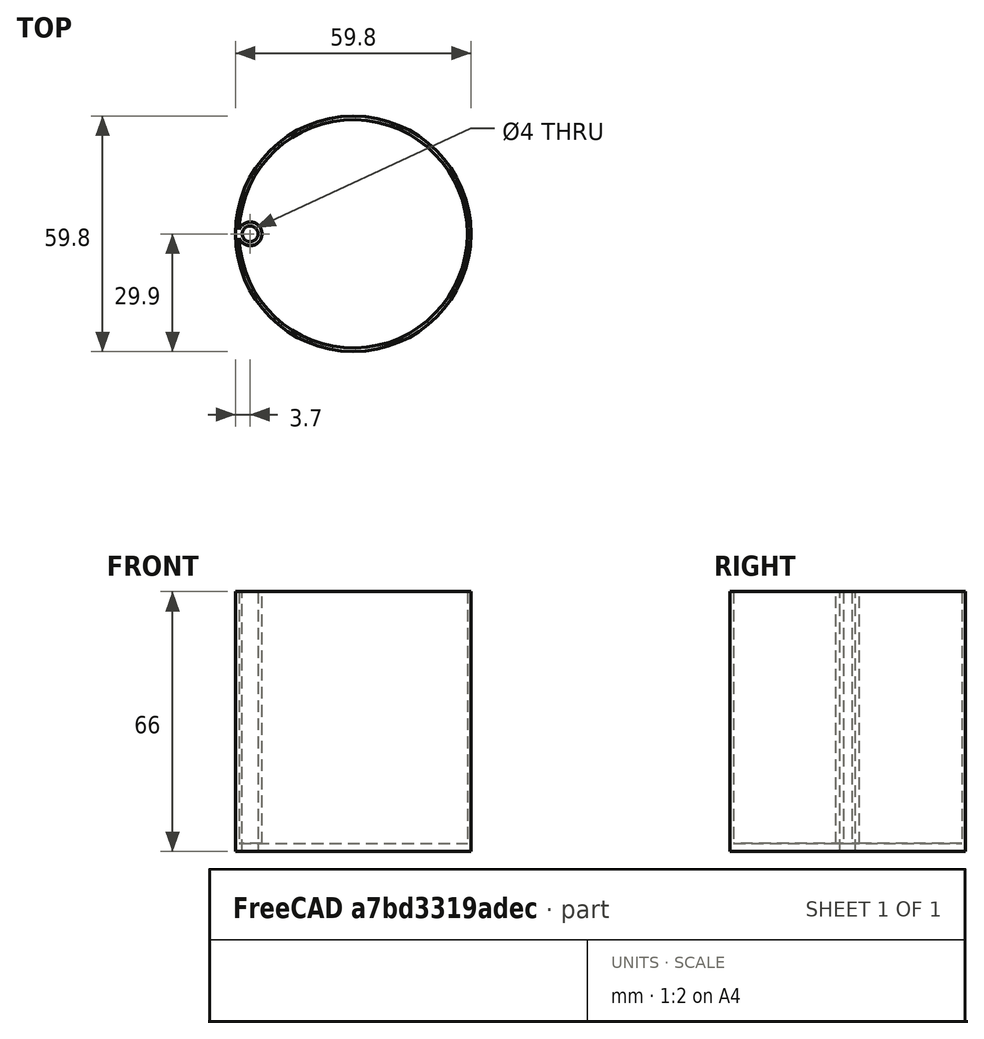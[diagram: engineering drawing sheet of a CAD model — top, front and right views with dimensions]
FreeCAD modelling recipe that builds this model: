
FCSTD DOCUMENT  (FreeCAD 1.0R38641 +468 (Git))
Label: piston_60
License: All rights reserved
LicenseURL: https://en.wikipedia.org/wiki/All_rights_reserved
objects: Sketcher::SketchObject×4, PartDesign::Pad×3, PartDesign::Pocket×1, PartDesign::Body×1, Mesh::Feature×1
note: 21 computed .brp shape members not serialized (recipe doc carries the construction recipe); baked Part::Feature solids carry a one-line shape summary decoded from their .brp

FEATURE [Sketcher::SketchObject] Sketch
  ArcFitTolerance = 1e-06
  AttachmentSupport = -> [XY_Plane]
  FullyConstrained = true
  MakeInternals = false
  MapMode = 5
  sketch-geometry (1):
    g0: Circle CenterX=0 CenterY=0 CenterZ=0 NormalX=0 NormalY=0 NormalZ=1 AngleXU=0 Radius=29.9
  constraints (2):
    c: Diameter(g0) = 59.8
    c: Coincident(g0,g-1)
FEATURE [PartDesign::Pad] Pad
  Direction = (0,0,1)
  Length = 2
  Length2 = 10
  Profile = -> Sketch
  ReferenceAxis = -> Sketch [N_Axis]
  Refine = true
  Suppressed = false
  Type = 0
FEATURE [Sketcher::SketchObject] Sketch001
  ArcFitTolerance = 1e-06
  AttachmentSupport = -> [Pad]
  ExternalGeometry = -> [Pad]
  FullyConstrained = true
  MakeInternals = false
  MapMode = 5
  Placement = pos=(0,0,2) rot=(0,0,1;0rad)
  sketch-geometry (2):
    g0: Circle CenterX=0 CenterY=0 CenterZ=0 NormalX=0 NormalY=0 NormalZ=1 AngleXU=0 Radius=29.9
    g1: Circle CenterX=0 CenterY=0 CenterZ=0 NormalX=0 NormalY=0 NormalZ=1 AngleXU=0 Radius=29
  constraints (4):
    c: Diameter(g0) = 59.8
    c: Coincident(g0,g-1)
    c: Diameter(g1) = 58
    c: Coincident(g1,g0)
FEATURE [PartDesign::Pad] Pad001
  BaseFeature = -> Pad
  Direction = (0,0,1)
  Length = 64
  Length2 = 10
  Profile = -> Sketch001
  ReferenceAxis = -> Sketch001 [N_Axis]
  Refine = true
  Suppressed = false
  Type = 0
FEATURE [Sketcher::SketchObject] Sketch002
  ArcFitTolerance = 1e-06
  AttachmentSupport = -> [Pad001]
  FullyConstrained = true
  MakeInternals = false
  MapMode = 5
  Placement = pos=(0,0,66) rot=(0,0,1;0rad)
  sketch-geometry (1):
    g0: Circle CenterX=-26.2 CenterY=0 CenterZ=0 NormalX=0 NormalY=0 NormalZ=1 AngleXU=0 Radius=3
  constraints (3):
    c: Diameter(g0) = 6
    c: PointOnObject(g0,g-1)
    c: DistanceX(g0,g-1) = 26.2
FEATURE [PartDesign::Pad] Pad002
  BaseFeature = -> Pad001
  Direction = (0,0,1)
  Length = 64
  Length2 = 10
  Profile = -> Sketch002
  ReferenceAxis = -> Sketch002 [N_Axis]
  Refine = true
  Reversed = true
  Suppressed = false
  Type = 0
FEATURE [Sketcher::SketchObject] Sketch003
  ArcFitTolerance = 1e-06
  AttachmentSupport = -> [Pad002]
  ExternalGeometry = -> [Pad002]
  FullyConstrained = true
  MakeInternals = false
  MapMode = 5
  Placement = pos=(0,0,66) rot=(0,0,1;0rad)
  sketch-geometry (1):
    g0: Circle CenterX=-26.2 CenterY=0 CenterZ=0 NormalX=0 NormalY=0 NormalZ=1 AngleXU=0 Radius=2
  constraints (2):
    c: Diameter(g0) = 4
    c: Coincident(g0,g-3)
FEATURE [PartDesign::Pocket] Pocket
  BaseFeature = -> Pad002
  Direction = (0,0,-1)
  Length = 5
  Length2 = 5
  Profile = -> Sketch003
  ReferenceAxis = -> Sketch003 [N_Axis]
  Refine = true
  Suppressed = false
  Type = 1
FEATURE [PartDesign::Body] Body  label="Corps"
  AllowCompound = false
  Group = -> [Sketch,Pad,Sketch001,Pad001,Sketch002,Pad002,Sketch003,Pocket]
  Origin = -> Origin
  Tip = -> Pocket
FEATURE [Mesh::Feature] Mesh  label="Pocket (Meshed)"
